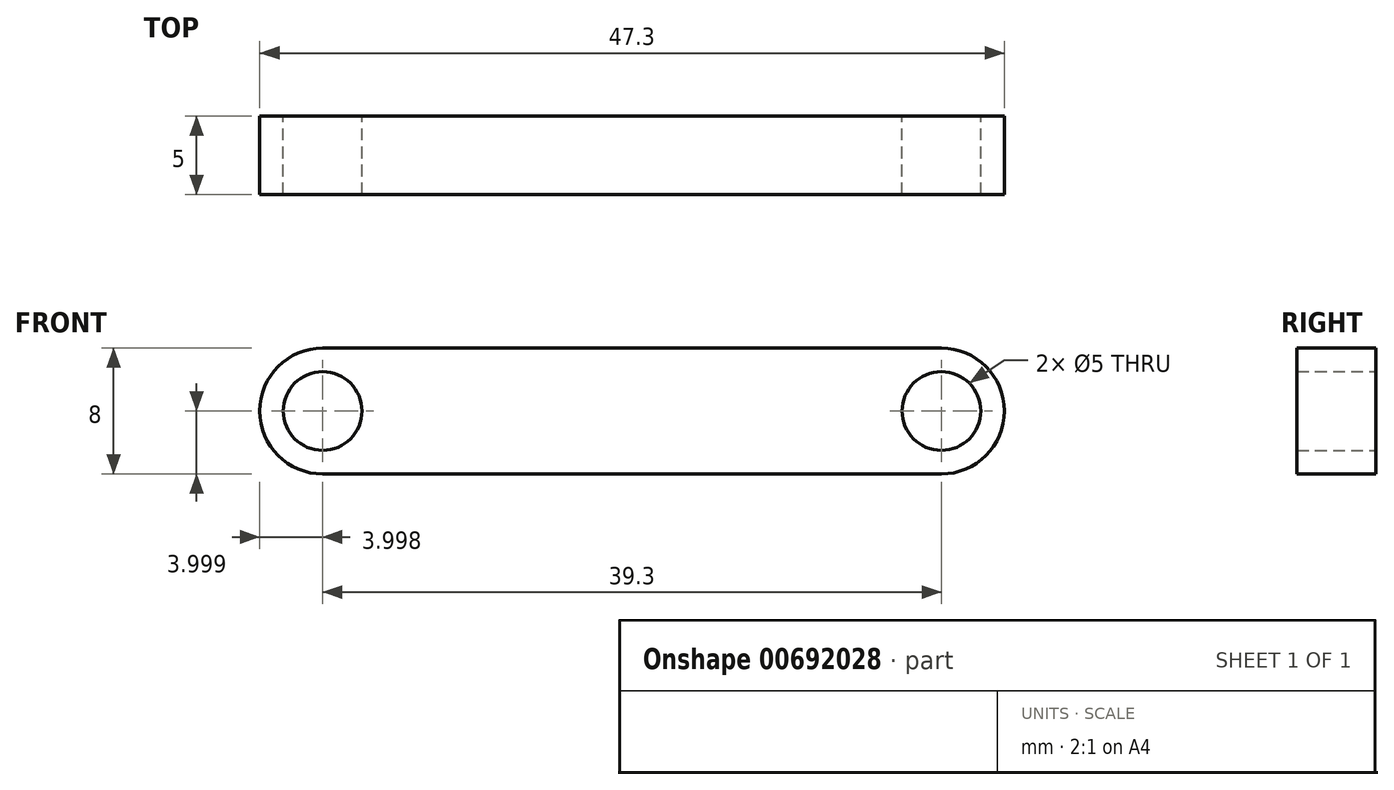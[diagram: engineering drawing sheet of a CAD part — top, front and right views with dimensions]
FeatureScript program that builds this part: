
annotation { "Feature Type Name" : "Feature", "Feature Type Description" : "" }
export const myFeature = defineFeature(function(context is Context, id is Id, definition is map)
    precondition{}
    {
        {
            var Q0;
            Q0=qCreatedBy(makeId("Front.planeOp"),FACE);
            var sketch = newSketch(context, id + "F0", { "sketchPlane" : qUnion([Q0])});
            skLineSegment(sketch, "E0.bottom", {"start": v(-38.2, 8.45) * mm, "end": v(1.1, 8.45) * mm});
            skLineSegment(sketch, "E0.top", {"start": v(-38.2, 0.45) * mm, "end": v(1.1, 0.45) * mm});
            skArc(sketch, "E1", {"start": v(-38.2, 8.45) * mm, "mid": v(-42.2, 4.45) * mm, "end": v(-38.2, 0.45) * mm});
            skArc(sketch, "E2", {"start": v(1.1, 0.45) * mm, "mid": v(5.1, 4.45) * mm, "end": v(1.1, 8.45) * mm});
            skCircle(sketch, "E3", {"center": v(-38.2, 4.45) * mm, "radius": 2.5 * mm});
            skCircle(sketch, "E4", {"center": v(1.1, 4.45) * mm, "radius": 2.5 * mm});
            skSolve(sketch);
        }
        {
            var Q0;
            Q0=makeQuery(id+"F0.imprint","IMPRINT",FACE,{"disambiguationData":[TD([[makeQuery(id+"F0.imprint","IMPRINT",EDGE,{"derivedFrom":sQuery(id+"F0.wireOp",EDGE,"E0.bottom")}),-1.0]])]});
            extrude(context, id + "F1", {"entities" : qUnion([Q0]), "depth" : 5 * mm, "offsetDistance" : 25 * mm});
        }
    });
